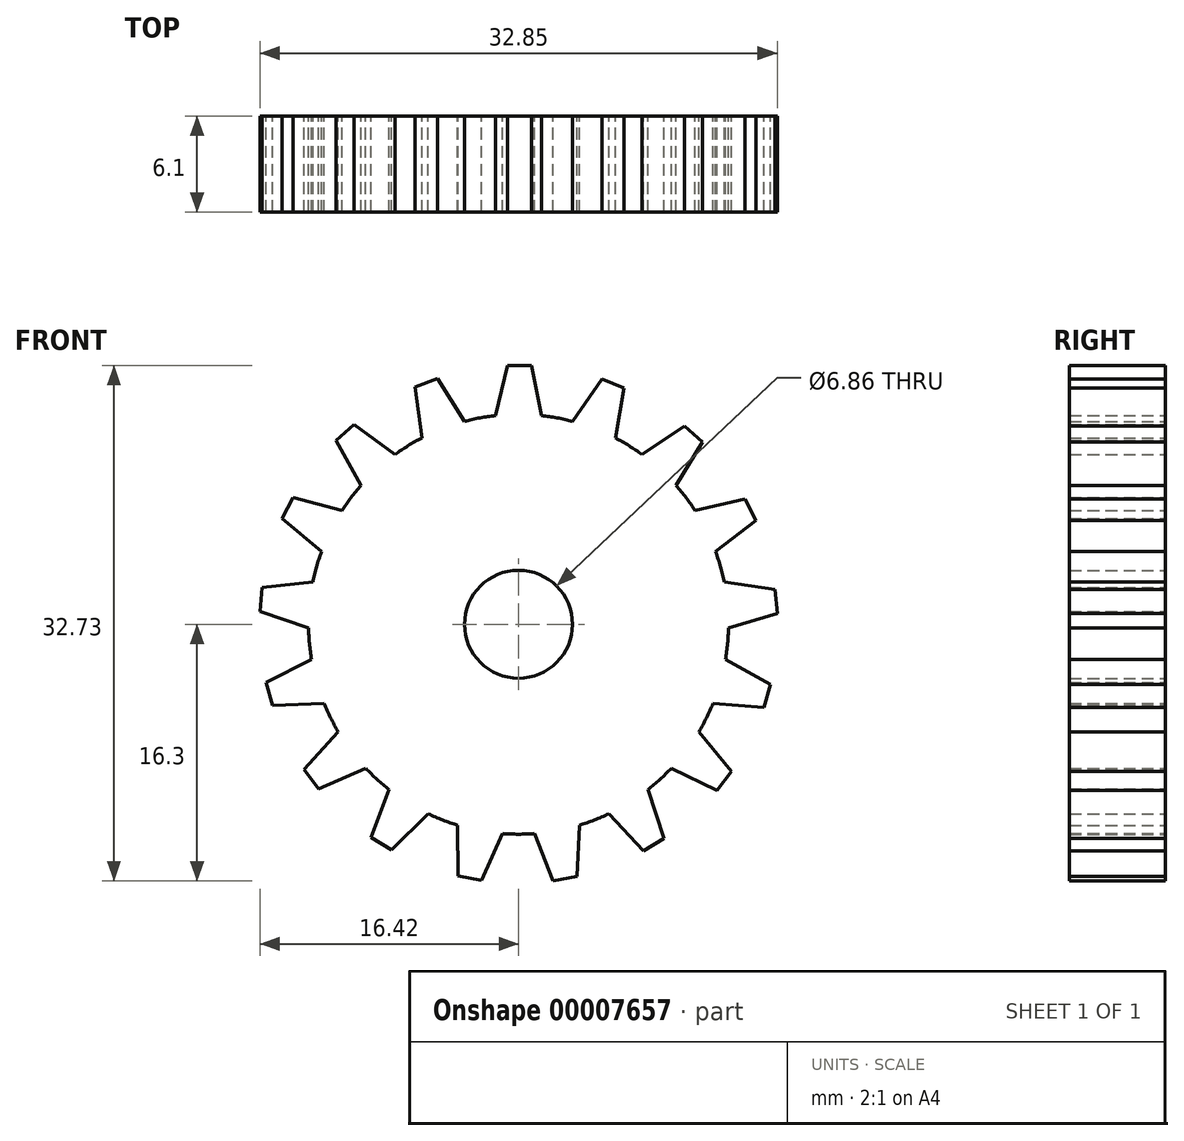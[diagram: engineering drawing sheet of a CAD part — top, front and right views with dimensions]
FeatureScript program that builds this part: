
annotation { "Feature Type Name" : "Feature", "Feature Type Description" : "" }
export const myFeature = defineFeature(function(context is Context, id is Id, definition is map)
    precondition{}
    {
        {
            var Q0;
            Q0=qCreatedBy(makeId("Front.planeOp"),FACE);
            var sketch = newSketch(context, id + "F0", { "sketchPlane" : qUnion([Q0])});
            skArc(sketch, "E0", {"start": v(7.86, 10.78) * mm, "mid": v(7.02, 11.34) * mm, "end": v(6.14, 11.83) * mm});
            skCircle(sketch, "E1", {"center": v(0, 0) * mm, "radius": 3.43 * mm});
            skLineSegment(sketch, "E2", {"start": v(1.45, 13.26) * mm, "end": v(0.83, 16.43) * mm});
            skLineSegment(sketch, "E3", {"start": v(0.83, 16.43) * mm, "end": v(-0.7, 16.43) * mm});
            skLineSegment(sketch, "E4", {"start": v(-0.7, 16.43) * mm, "end": v(-1.45, 13.26) * mm});
            skLineSegment(sketch, "E5.1.0", {"start": v(-6.58, 15.07) * mm, "end": v(-6.14, 11.83) * mm});
            skLineSegment(sketch, "E5.1.1", {"start": v(-3.43, 12.89) * mm, "end": v(-5.16, 15.62) * mm});
            skLineSegment(sketch, "E5.1.2", {"start": v(-5.16, 15.62) * mm, "end": v(-6.58, 15.07) * mm});
            skLineSegment(sketch, "E5.2.0", {"start": v(-11.58, 11.67) * mm, "end": v(-10, 8.82) * mm});
            skLineSegment(sketch, "E5.2.1", {"start": v(-7.86, 10.78) * mm, "end": v(-10.45, 12.7) * mm});
            skLineSegment(sketch, "E5.2.2", {"start": v(-10.45, 12.7) * mm, "end": v(-11.58, 11.67) * mm});
            skLineSegment(sketch, "E5.3.0", {"start": v(-15.01, 6.7) * mm, "end": v(-12.51, 4.6) * mm});
            skLineSegment(sketch, "E5.3.1", {"start": v(-11.22, 7.21) * mm, "end": v(-14.33, 8.07) * mm});
            skLineSegment(sketch, "E5.3.2", {"start": v(-14.33, 8.07) * mm, "end": v(-15.01, 6.7) * mm});
            skLineSegment(sketch, "E5.4.0", {"start": v(-16.42, 0.83) * mm, "end": v(-13.33, -0.23) * mm});
            skLineSegment(sketch, "E5.4.1", {"start": v(-13.06, 2.67) * mm, "end": v(-16.28, 2.34) * mm});
            skLineSegment(sketch, "E5.4.2", {"start": v(-16.28, 2.34) * mm, "end": v(-16.42, 0.83) * mm});
            skLineSegment(sketch, "E5.5.0", {"start": v(-15.6, -5.16) * mm, "end": v(-12.35, -5.03) * mm});
            skLineSegment(sketch, "E5.5.1", {"start": v(-13.15, -2.23) * mm, "end": v(-16.03, -3.7) * mm});
            skLineSegment(sketch, "E5.5.2", {"start": v(-16.03, -3.7) * mm, "end": v(-15.6, -5.16) * mm});
            skLineSegment(sketch, "E5.6.0", {"start": v(-12.7, -10.45) * mm, "end": v(-9.7, -9.15) * mm});
            skLineSegment(sketch, "E5.6.1", {"start": v(-11.45, -6.83) * mm, "end": v(-13.6, -9.24) * mm});
            skLineSegment(sketch, "E5.6.2", {"start": v(-13.6, -9.24) * mm, "end": v(-12.7, -10.45) * mm});
            skLineSegment(sketch, "E5.7.0", {"start": v(-8.06, -14.33) * mm, "end": v(-5.74, -12.04) * mm});
            skLineSegment(sketch, "E5.7.1", {"start": v(-8.21, -10.5) * mm, "end": v(-9.35, -13.53) * mm});
            skLineSegment(sketch, "E5.7.2", {"start": v(-9.35, -13.53) * mm, "end": v(-8.06, -14.33) * mm});
            skLineSegment(sketch, "E5.8.0", {"start": v(-2.34, -16.27) * mm, "end": v(-1, -13.3) * mm});
            skLineSegment(sketch, "E5.8.1", {"start": v(-3.87, -12.76) * mm, "end": v(-3.84, -16) * mm});
            skLineSegment(sketch, "E5.8.2", {"start": v(-3.84, -16) * mm, "end": v(-2.34, -16.27) * mm});
            skLineSegment(sketch, "E5.9.0", {"start": v(3.7, -16.02) * mm, "end": v(3.87, -12.76) * mm});
            skLineSegment(sketch, "E5.9.1", {"start": v(1, -13.3) * mm, "end": v(2.2, -16.3) * mm});
            skLineSegment(sketch, "E5.9.2", {"start": v(2.2, -16.3) * mm, "end": v(3.7, -16.02) * mm});
            skLineSegment(sketch, "E5.10.0", {"start": v(9.24, -13.6) * mm, "end": v(8.21, -10.5) * mm});
            skLineSegment(sketch, "E5.10.1", {"start": v(5.74, -12.04) * mm, "end": v(7.94, -14.4) * mm});
            skLineSegment(sketch, "E5.10.2", {"start": v(7.94, -14.4) * mm, "end": v(9.24, -13.6) * mm});
            skLineSegment(sketch, "E5.11.0", {"start": v(13.53, -9.35) * mm, "end": v(11.45, -6.83) * mm});
            skLineSegment(sketch, "E5.11.1", {"start": v(9.7, -9.15) * mm, "end": v(12.6, -10.56) * mm});
            skLineSegment(sketch, "E5.11.2", {"start": v(12.6, -10.56) * mm, "end": v(13.53, -9.35) * mm});
            skLineSegment(sketch, "E5.12.0", {"start": v(15.99, -3.83) * mm, "end": v(13.15, -2.23) * mm});
            skLineSegment(sketch, "E5.12.1", {"start": v(12.35, -5.03) * mm, "end": v(15.57, -5.3) * mm});
            skLineSegment(sketch, "E5.12.2", {"start": v(15.57, -5.3) * mm, "end": v(15.99, -3.83) * mm});
            skLineSegment(sketch, "E5.13.0", {"start": v(16.3, 2.2) * mm, "end": v(13.06, 2.67) * mm});
            skLineSegment(sketch, "E5.13.1", {"start": v(13.33, -0.23) * mm, "end": v(16.43, 0.69) * mm});
            skLineSegment(sketch, "E5.13.2", {"start": v(16.43, 0.69) * mm, "end": v(16.3, 2.2) * mm});
            skLineSegment(sketch, "E5.14.0", {"start": v(14.4, 7.94) * mm, "end": v(11.22, 7.21) * mm});
            skLineSegment(sketch, "E5.14.1", {"start": v(12.51, 4.6) * mm, "end": v(15.08, 6.58) * mm});
            skLineSegment(sketch, "E5.14.2", {"start": v(15.08, 6.58) * mm, "end": v(14.4, 7.94) * mm});
            skLineSegment(sketch, "E5.14.3", {"start": v(11.22, 7.21) * mm, "end": v(12.51, 4.6) * mm});
            skLineSegment(sketch, "E5.15.0", {"start": v(10.55, 12.6) * mm, "end": v(7.86, 10.78) * mm});
            skLineSegment(sketch, "E5.15.1", {"start": v(10, 8.82) * mm, "end": v(11.68, 11.58) * mm});
            skLineSegment(sketch, "E5.15.2", {"start": v(11.68, 11.58) * mm, "end": v(10.55, 12.6) * mm});
            skLineSegment(sketch, "E5.16.0", {"start": v(5.29, 15.57) * mm, "end": v(3.43, 12.89) * mm});
            skLineSegment(sketch, "E5.16.1", {"start": v(6.14, 11.83) * mm, "end": v(6.7, 15.02) * mm});
            skLineSegment(sketch, "E5.16.2", {"start": v(6.7, 15.02) * mm, "end": v(5.29, 15.57) * mm});
            skArc(sketch, "E6.trimOffspring", {"start": v(3.43, 12.89) * mm, "mid": v(2.45, 13.1) * mm, "end": v(1.45, 13.26) * mm});
            skArc(sketch, "E7.trimOffspring", {"start": v(-1.45, 13.26) * mm, "mid": v(-2.45, 13.1) * mm, "end": v(-3.43, 12.89) * mm});
            skArc(sketch, "E8.trimOffspring", {"start": v(-10, 8.82) * mm, "mid": v(-10.64, 8.04) * mm, "end": v(-11.22, 7.21) * mm});
            skArc(sketch, "E9.trimOffspring", {"start": v(-6.14, 11.83) * mm, "mid": v(-7.02, 11.34) * mm, "end": v(-7.86, 10.78) * mm});
            skArc(sketch, "E10.trimOffspring", {"start": v(-12.51, 4.6) * mm, "mid": v(-12.83, 3.65) * mm, "end": v(-13.06, 2.67) * mm});
            skArc(sketch, "E11.trimOffspring", {"start": v(-13.33, -0.23) * mm, "mid": v(-13.28, -1.23) * mm, "end": v(-13.15, -2.23) * mm});
            skArc(sketch, "E12.trimOffspring", {"start": v(-12.35, -5.03) * mm, "mid": v(-11.94, -5.94) * mm, "end": v(-11.45, -6.83) * mm});
            skArc(sketch, "E13.trimOffspring", {"start": v(-9.7, -9.15) * mm, "mid": v(-8.98, -9.85) * mm, "end": v(-8.21, -10.5) * mm});
            skArc(sketch, "E14.trimOffspring", {"start": v(-5.74, -12.04) * mm, "mid": v(-4.82, -12.43) * mm, "end": v(-3.87, -12.76) * mm});
            skArc(sketch, "E15.trimOffspring", {"start": v(-1, -13.3) * mm, "mid": v(0, -13.34) * mm, "end": v(1, -13.3) * mm});
            skArc(sketch, "E16.trimOffspring", {"start": v(3.87, -12.76) * mm, "mid": v(4.82, -12.43) * mm, "end": v(5.74, -12.04) * mm});
            skArc(sketch, "E17.trimOffspring", {"start": v(8.21, -10.5) * mm, "mid": v(8.98, -9.85) * mm, "end": v(9.7, -9.15) * mm});
            skArc(sketch, "E18.trimOffspring", {"start": v(11.45, -6.83) * mm, "mid": v(11.94, -5.94) * mm, "end": v(12.35, -5.03) * mm});
            skArc(sketch, "E19.trimOffspring", {"start": v(13.15, -2.23) * mm, "mid": v(13.28, -1.23) * mm, "end": v(13.33, -0.23) * mm});
            skArc(sketch, "E20.trimOffspring", {"start": v(13.06, 2.67) * mm, "mid": v(11.94, 5.94) * mm, "end": v(10, 8.82) * mm});
            skSolve(sketch);
        }
        {
            var Q0;
            Q0 = qSketchRegion(id + "F0", true);
            extrude(context, id + "F1", {"entities" : qUnion([Q0]), "depth" : 6.1 * mm});
        }
    });
